# Revit family: 03_MAGIS40-33_PB1A
name_source: partatom
category: Porte
units: mm (PartAtom-declared; Revit-internal decimal feet)

## family parameters
Condiviso = No
Host = Muro
Numero OmniClass = 23.30.10.00
Punto di calcolo locali = No
Sempre verticale = Sì
Taglio con vuoti quando caricato = No
Titolo OmniClass = Doors

## types (3) — shared parameters
Chiusura muro = Per host
Codice assieme = B2030100
Costruzione analitica = <Nessuno>
EXTERNAL ALUMINUM FRAME/TELAIO ALLUMINIO ESTERNO = UNIFORM_ALUMINUM
Funzione = Interno
GLASS WEIGHT/PESO VETRO = 30.00 kg/m²
HANDLE/MANIGLIA = UNIFORM_ALUMINUM
INTERIOR WOOD FRAME/TELAIO LEGNO INTERNO = UNIFORM_WOOD
Larghezza telaio = 75 mm
MAXIMUM HEIGHT/ALTEZZA MASSIMA = 2500 mm
MAXIMUM WIDTH/LARGHEZZA MASSIMA = 1000 mm  [stored 3.28084 ft]
MINIMUM HEIGHT/ALTEZZA MINIMA = 1800 mm
MINIMUM WIDTH/LARGHEZZA MINIMA  = 500 mm  [stored 1.64042 ft]
Modello = MAGIS40
PRODUCER WEBSITE/SITO WEB PRODUTTORE = www.uniform.it
PRODUCT WEBSITE/SITO WEB PRODOTTO = www.sistema-uni-one.it
Proiezione telaio est. = 25 mm  [stored 0.082021 ft]
Proiezione telaio int. = 25 mm  [stored 0.082021 ft]
W = 1000 mm  [stored 3.28084 ft]
WINDOW GLASS/VETRO FINESTRA = UNIFORM_GLASS
zero-valued in all types: Rw GLASS/Rw VETRO, Rw WINDOW/Rw FINESTRA

## per-type parameters (varying)
| type | Altezza | H | HANDLE HEIGHT/ALTEZZA MANIGLIA | Larghezza | MAX_DIMENSIONS_WARNING | Ug GLASS/Ug VETRO | Uw WINDOW/Uw FINESTRA | V1 | V2 |
| ACOUSTIC | 2100 mm | 2100 mm | 1100 mm | 1000 mm  [stored 3.28084 ft] | No | 0.5000 W/(m²·K) | 1.1000 W/(m²·K) | 2050 mm | 2070 mm |
| THERMAL | 2000 mm  [stored 6.56168 ft] | 2000 mm  [stored 6.56168 ft] | 1100 mm | 1500 mm | Sì | 1.0000 W/(m²·K) | 1.4000 W/(m²·K) | 1950 mm  [stored 6.39764 ft] | 1970 mm  [stored 6.46325 ft] |
| THERMAL_PERFORMANCE | 2000 mm  [stored 6.56168 ft] | 2000 mm  [stored 6.56168 ft] | 1000 mm  [stored 3.28084 ft] | 1500 mm | Sì | 0.5000 W/(m²·K) | 1.1000 W/(m²·K) | 1950 mm  [stored 6.39764 ft] | 1970 mm  [stored 6.46325 ft] |

note: [stored X ft] marks values corroborated as IEEE doubles in the binary element streams (Revit-internal decimal feet)
